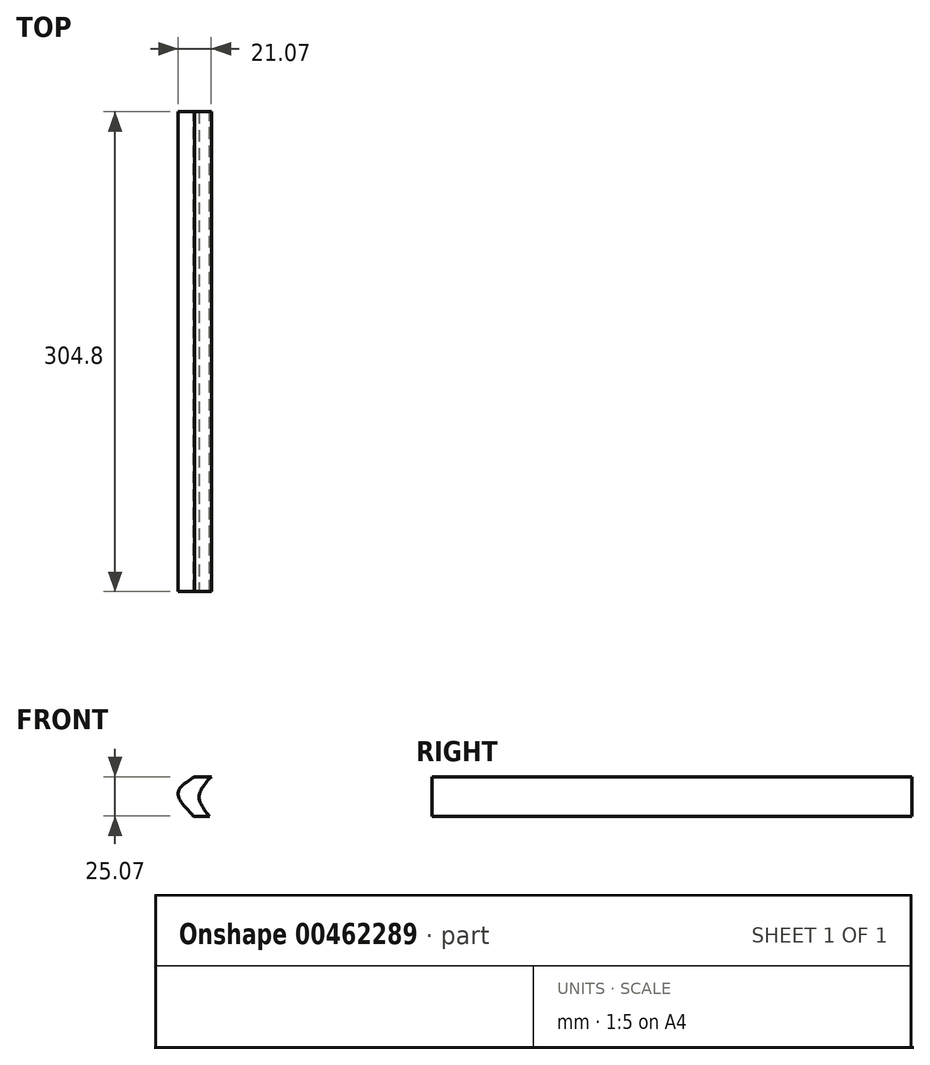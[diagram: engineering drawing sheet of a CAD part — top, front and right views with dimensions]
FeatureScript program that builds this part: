
annotation { "Feature Type Name" : "Feature", "Feature Type Description" : "" }
export const myFeature = defineFeature(function(context is Context, id is Id, definition is map)
    precondition{}
    {
        {
            var Q0;
            Q0=qCreatedBy(makeId("Front.planeOp"),FACE);
            var sketch = newSketch(context, id + "F0", { "sketchPlane" : qUnion([Q0])});
            skFitSpline(sketch, "E0", {"points": [v(16.1, 17.18) * mm, v(8.36, 4.49) * mm, v(14.86, -7.9) * mm], "startDerivative": vector(-22.46, -24.96) * mm, "endDerivative": vector(20.2, -25.18) * mm});
            skLineSegment(sketch, "E1", {"start": v(16.1, 17.18) * mm, "end": v(5.57, 17.18) * mm});
            skLineSegment(sketch, "E2", {"start": v(14.86, -7.9) * mm, "end": v(4.95, -7.9) * mm});
            skFitSpline(sketch, "E3", {"points": [v(5.57, 17.18) * mm, v(-4.95, 6.96) * mm, v(4.95, -7.9) * mm], "startDerivative": vector(-31.89, -19.86) * mm, "endDerivative": vector(29.64, -30.11) * mm});
            skSolve(sketch);
        }
        {
            var Q0;
            Q0=makeQuery(id+"F0.imprint","IMPRINT",FACE,{"disambiguationData":[TD([[makeQuery(id+"F0.imprint","IMPRINT",EDGE,{"derivedFrom":sQuery(id+"F0.wireOp",EDGE,"E0")}),-1.0]])]});
            extrude(context, id + "F1", {"entities" : qUnion([Q0]), "depth" : 304.8 * mm});
        }
    });
